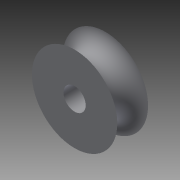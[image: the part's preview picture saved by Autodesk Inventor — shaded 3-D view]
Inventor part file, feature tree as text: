
AUTODESK INVENTOR PART (.ipt)
format: ipt  version: 2015 (Build 190159000, 159)  size: 144,384 bytes
history: native  units: in
note: dims shown in document units (in); Inventor stores cm internally (conversion verified against a paired STEP export)
features: sketch x3, revolve x2, extrude x1
ambient origin geometry x8: Origin, YZ Plane, XZ Plane, XY Plane, X Axis, Y Axis, Z Axis, Center Point
bodies: Solid1 (feature_tree)
feature tree (6):
  revolve  "Revolution1"  [1 undecoded]
  extrude  "Extrusion1"  Depth=0.4882in
  revolve  "Revolution2"  Angle=90.0deg
  sketch  "Sketch1"  dims[d0=90.0deg d1=0.3125in]
  sketch  "Sketch2"  dims[d2=1.0in d3=0.0in d4=0.4882in]
  sketch  "Sketch4"  dims[d5=0.6in d9=90.0deg]
note: 1 required parameter value undecoded (feature->parameter linkage not recoverable at this tier; creation-order binding heuristic only, values carry confidence <= 0.55)
